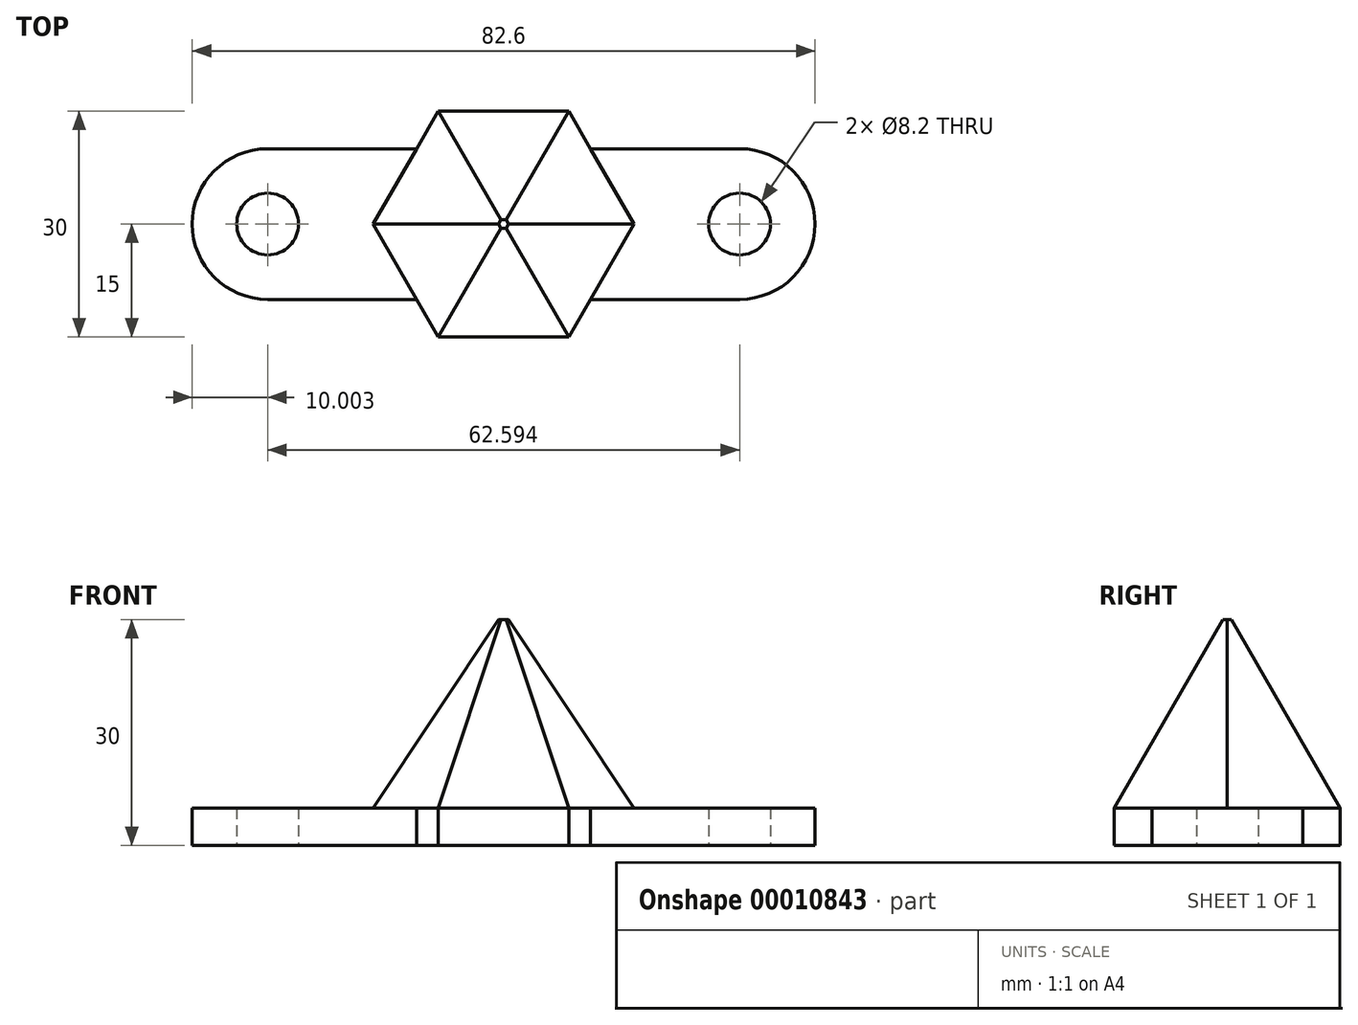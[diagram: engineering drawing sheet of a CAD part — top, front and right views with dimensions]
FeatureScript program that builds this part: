
annotation { "Feature Type Name" : "Feature", "Feature Type Description" : "" }
export const myFeature = defineFeature(function(context is Context, id is Id, definition is map)
    precondition{}
    {
        {
            var Q0;
            Q0=qCreatedBy(makeId("Top.planeOp"),FACE);
            var sketch = newSketch(context, id + "F0", { "sketchPlane" : qUnion([Q0])});
            skCircle(sketch, "E0", {"center": v(-31.3, 0) * mm, "radius": 4.1 * mm});
            skCircle(sketch, "E1", {"center": v(31.3, 0) * mm, "radius": 4.1 * mm});
            skLineSegment(sketch, "E2.rect.bottom", {"start": v(-31.3, 10) * mm, "end": v(31.3, 10) * mm});
            skLineSegment(sketch, "E2.rect.top", {"start": v(-31.3, -10) * mm, "end": v(31.3, -10) * mm});
            skLineSegment(sketch, "E2.rect.left", {"start": v(-41.3, 0) * mm, "end": v(-41.3, 0) * mm});
            skLineSegment(sketch, "E2.rect.right", {"start": v(41.3, 0) * mm, "end": v(41.3, 0) * mm});
            skPoint(sketch, "E2.rect.middle", {"position": v(0, 0) * mm});
            skPoint(sketch, "E3.visualSharp", {"position": v(-41.3, 10) * mm});
            skArc(sketch, "E3.filletArc", {"start": v(-31.3, 10) * mm, "mid": v(-38.37, 7.07) * mm, "end": v(-41.3, 0) * mm});
            skPoint(sketch, "E4.visualSharp", {"position": v(-41.3, -10) * mm});
            skArc(sketch, "E4.filletArc", {"start": v(-41.3, 0) * mm, "mid": v(-38.37, -7.07) * mm, "end": v(-31.3, -10) * mm});
            skPoint(sketch, "E5.visualSharp", {"position": v(41.3, 10) * mm});
            skArc(sketch, "E5.filletArc", {"start": v(41.3, 0) * mm, "mid": v(38.37, 7.07) * mm, "end": v(31.3, 10) * mm});
            skPoint(sketch, "E6.visualSharp", {"position": v(41.3, -10) * mm});
            skArc(sketch, "E6.filletArc", {"start": v(31.3, -10) * mm, "mid": v(38.37, -7.07) * mm, "end": v(41.3, 0) * mm});
            skSolve(sketch);
        }
        {
            var Q0;
            Q0=makeQuery(id+"F0.imprint","IMPRINT",FACE,{"disambiguationData":[TD([[makeQuery(id+"F0.imprint","IMPRINT",EDGE,{"derivedFrom":sQuery(id+"F0.wireOp",EDGE,"E0")}),-1.0]])]});
            extrude(context, id + "F1", {"entities" : qUnion([Q0]), "depth" : 5 * mm});
        }
        {
            var Q0;
            Q0=makeQuery(id+"F1.opExtrude","CAP_FACE",FACE,{"disambiguationData":[OSD([sQuery(id+"F0.wireOp",EDGE,"E0"),sQuery(id+"F0.wireOp",EDGE,"E1"),sQuery(id+"F0.wireOp",EDGE,"E2.rect.bottom"),sQuery(id+"F0.wireOp",EDGE,"E2.rect.top"),sQuery(id+"F0.wireOp",EDGE,"E3.filletArc"),sQuery(id+"F0.wireOp",EDGE,"E4.filletArc"),sQuery(id+"F0.wireOp",EDGE,"E5.filletArc"),sQuery(id+"F0.wireOp",EDGE,"E6.filletArc")])],"isStart":false});
            var sketch = newSketch(context, id + "F2", { "sketchPlane" : qUnion([Q0])});
            skCircle(sketch, "E7.cCircle", {"center": v(0, 0) * mm, "radius": 15 * mm, "construction": true});
            skLineSegment(sketch, "E7.0", {"start": v(-8.66, 15) * mm, "end": v(8.66, 15) * mm});
            skLineSegment(sketch, "E7.1", {"start": v(8.66, 15) * mm, "end": v(17.32, 0) * mm});
            skLineSegment(sketch, "E7.2", {"start": v(17.32, 0) * mm, "end": v(8.66, -15) * mm});
            skLineSegment(sketch, "E7.3", {"start": v(8.66, -15) * mm, "end": v(-8.66, -15) * mm});
            skLineSegment(sketch, "E7.4", {"start": v(-8.66, -15) * mm, "end": v(-17.32, 0) * mm});
            skLineSegment(sketch, "E7.5", {"start": v(-17.32, 0) * mm, "end": v(-8.66, 15) * mm});
            skPoint(sketch, "E7.0.midPoint", {"position": v(0, 15) * mm});
            skSolve(sketch);
        }
        {
            var Q0;
            Q0=makeQuery(id+"F2.imprint","IMPRINT",FACE,{"disambiguationData":[TD([[makeQuery(id+"F2.imprint","IMPRINT",EDGE,{"derivedFrom":sQuery(id+"F2.wireOp",EDGE,"E7.0")}),-1.0]])]});
            var Q1;
            {var subQ3=sQuery(id+"F2.wireOp",EDGE,"E7.1");var subQ9=sQuery(id+"F2.wireOp",EDGE,"E7.2");var subQ11=makeQuery(id+"F2.imprint","INTERSECT",VERTEX,{"derivedFrom":[subQ3,subQ9]});Q1=makeQuery(id+"F2.imprint","IMPRINT",FACE,{"disambiguationData":[TD([[makeQuery(id+"F2.imprint","IMPRINT",EDGE,{"disambiguationData":[TD([[subQ11,1.0]])],"derivedFrom":subQ3}),-1.0]])]});}
            var Q2;
            {var subQ5=sQuery(id+"F2.wireOp",EDGE,"E7.3");Q2=makeQuery(id+"F2.imprint","IMPRINT",FACE,{"disambiguationData":[TD([[makeQuery(id+"F2.imprint","IMPRINT",EDGE,{"derivedFrom":subQ5}),-1.0]])]});}
            extrude(context, id + "F3", {"entities" : qUnion([Q0, Q1, Q2]), "operationType" : NewBodyOperationType.ADD, "depth" : 25 * mm, "hasDraft" : true, "draftAngle" : 30 * degree, "draftPullDirection" : true});
        }
        {
            var Q0;
            {var subQ0=sQuery(id+"F2.wireOp",EDGE,"E7.2");var subQ1=sQuery(id+"F2.wireOp",EDGE,"E7.3");var subQ2=sQuery(id+"F2.wireOp",EDGE,"E7.4");var subQ3=sQuery(id+"F0.wireOp",EDGE,"E2.rect.top");Q0=makeQuery(id+"F3.boolean.opBoolean","SPLIT",FACE,{"disambiguationData":[TD([makeQuery(id+"F1.opExtrude","SWEPT_FACE",FACE,{"disambiguationData":[OSD([subQ3])]})])],"derivedFrom":makeQuery(id+"F3.opExtrude","CAP_FACE",FACE,{"disambiguationData":[OSD([sQuery(id+"F2.wireOp",EDGE,"E7.0"),sQuery(id+"F2.wireOp",EDGE,"E7.1"),subQ0,subQ1,subQ2,sQuery(id+"F2.wireOp",EDGE,"E7.5")])],"isStart":true})});}
            var Q1;
            {var subQ0=sQuery(id+"F2.wireOp",EDGE,"E7.0");var subQ1=sQuery(id+"F2.wireOp",EDGE,"E7.1");var subQ2=sQuery(id+"F2.wireOp",EDGE,"E7.5");var subQ3=sQuery(id+"F0.wireOp",EDGE,"E2.rect.bottom");Q1=makeQuery(id+"F3.boolean.opBoolean","SPLIT",FACE,{"disambiguationData":[TD([makeQuery(id+"F1.opExtrude","SWEPT_FACE",FACE,{"disambiguationData":[OSD([subQ3])]})])],"derivedFrom":makeQuery(id+"F3.opExtrude","CAP_FACE",FACE,{"disambiguationData":[OSD([subQ0,subQ1,sQuery(id+"F2.wireOp",EDGE,"E7.2"),sQuery(id+"F2.wireOp",EDGE,"E7.3"),sQuery(id+"F2.wireOp",EDGE,"E7.4"),subQ2])],"isStart":true})});}
            var Q2;
            Q2=makeQuery(id+"F1.opExtrude","CAP_FACE",FACE,{"disambiguationData":[OSD([sQuery(id+"F0.wireOp",EDGE,"E0"),sQuery(id+"F0.wireOp",EDGE,"E1"),sQuery(id+"F0.wireOp",EDGE,"E2.rect.bottom"),sQuery(id+"F0.wireOp",EDGE,"E2.rect.top"),sQuery(id+"F0.wireOp",EDGE,"E3.filletArc"),sQuery(id+"F0.wireOp",EDGE,"E4.filletArc"),sQuery(id+"F0.wireOp",EDGE,"E5.filletArc"),sQuery(id+"F0.wireOp",EDGE,"E6.filletArc")])],"isStart":true});
            extrude(context, id + "F4", {"entities" : qUnion([Q0, Q1]), "operationType" : NewBodyOperationType.ADD, "endBound" : BoundingType.UP_TO_SURFACE, "endBoundEntityFace" : qUnion([Q2]), "depth" : 25 * mm});
        }
    });
